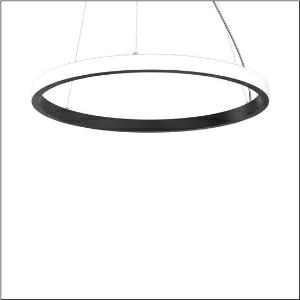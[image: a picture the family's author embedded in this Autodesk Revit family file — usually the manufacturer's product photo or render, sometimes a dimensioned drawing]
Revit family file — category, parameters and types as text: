
# Revit family: silica_r__21_ring-o_5pjbo4d1104a_942a
name_source: partatom
category: Lighting Fixtures
units: mm (PartAtom-declared; Revit-internal decimal feet)

## family parameters
Cut with Voids When Loaded = No
Host = Face
Light Source = No
Part Type = Normal
Room Calculation Point = No
Round Connector Dimension = Use Diameter
Shared = No

## types (1)
- Silica® 21 Ring-O (1 x LED, 8820 lm, 140 W, 3000K)
    Apparent Load = 140 VA
    CIE Flux Codes = 2 16 49 50 100
    Color Rendering = 80
    Color Temperature = 3000K
    Default Elevation = 1800 mm
    Description = Silica® 21 Ring-O, suspended luminaire, of PMMA, frosted, light emission: outer ring side luminous distribution, primary light characteristic: symmetric, installation type: suspended mounting, LED, rated luminous flux: 8.820lm, luminous efficacy: 63lm/W, light colour: 830, colour temperature: 3000K, with terminal, 5-pole, mains connection: 230V, AC/DC, 0/50..60Hz, rated input power: 140W, housing, of extruded aluminium section, jet black (RAL 9005), diameter: 1.480mm, ceiling canopy, jet black (RAL 9005), protection rating (lamp compartment): IP40, insulation class (complete): insulation class I (protective earthing), certification: CE, impact resistance: IK02, permissible operating ambient temperature: 0..+35°C, packaging unit: 1 piece
    Height = 48 mm  [stored 0.15748 ft]
    Lamp = 1 x LED
    Lamp Light Flux = 8820 lm
    Lamp Power = 140 W
    Lamp count = 1
    Length = 1480 mm
    Luminous efficacy = 63 lm/W
    Manufacturer = Siteco
    ModVariant = No
    Model = 5PJBO4D1104A
    Mounting Place = Ceiling
    Mounting Type = Pendant
    Number of Poles = 1
    OnlyDefault = Yes
    Power Factor = 1
    Product Name = Silica® 21 Ring-O
    Product group = suspended luminaire
    ProductGroupID = 904
    Protection Class = Protection class I
    Protection Degree = Degree of protection
    RLX_Detail_Level = 1
    RLX_Emergency_Light_Flux = 0 lm
    RLX_Emergency_Type = 0
    RLX_Emergency_Type_DB = No
    RlxData = <blob elided: 20537 chars, md5=2af3621d>
    Socket = socket
    Standby Power = 0 W
    System Light Flux = 8820 lm
    System Power = 140 W
    Type Comments = Product without accessories
    Type Image = l_1258389.jpg
    URL = http://relux.com
    VarID = ---
    Voltage = 0 V
    Weight = 0.00 kg
    Width = 0 mm  [stored 0 ft]

note: [stored X ft] marks values corroborated as IEEE doubles in the binary element streams (Revit-internal decimal feet)

## geometry (parser evidence)
native form markers: Blend x4, Sweep x12
no freeform markers — native parametric forms only
